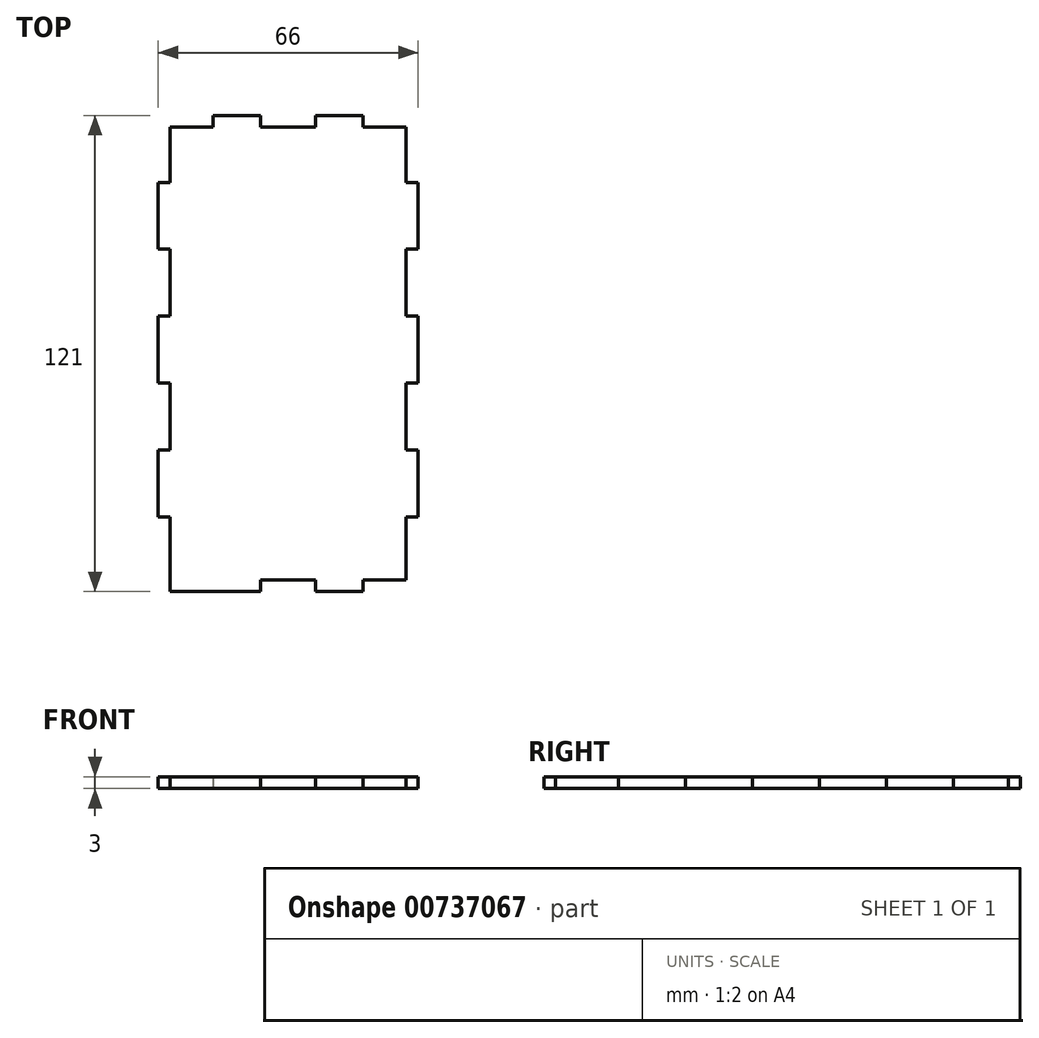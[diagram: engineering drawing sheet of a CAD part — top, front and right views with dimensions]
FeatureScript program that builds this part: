
annotation { "Feature Type Name" : "Feature", "Feature Type Description" : "" }
export const myFeature = defineFeature(function(context is Context, id is Id, definition is map)
    precondition{}
    {
        {
            var Q0;
            Q0=qCreatedBy(makeId("Top.planeOp"),FACE);
            var sketch = newSketch(context, id + "F0", { "sketchPlane" : qUnion([Q0])});
            skLineSegment(sketch, "E0.bottom", {"start": v(33, -60.5) * mm, "end": v(-33, -60.5) * mm, "construction": true});
            skLineSegment(sketch, "E0.top", {"start": v(33, 60.5) * mm, "end": v(-33, 60.5) * mm, "construction": true});
            skLineSegment(sketch, "E0.left", {"start": v(33, -60.5) * mm, "end": v(33, 60.5) * mm, "construction": true});
            skLineSegment(sketch, "E0.right", {"start": v(-33, -60.5) * mm, "end": v(-33, 60.5) * mm, "construction": true});
            skPoint(sketch, "E0.middle", {"position": v(0, 0) * mm});
            skLineSegment(sketch, "E1", {"start": v(-30, 57.5) * mm, "end": v(-19, 57.5) * mm});
            skLineSegment(sketch, "E2", {"start": v(-19, 57.5) * mm, "end": v(-19, 60.5) * mm});
            skLineSegment(sketch, "E3", {"start": v(-19, 60.5) * mm, "end": v(-7, 60.5) * mm});
            skLineSegment(sketch, "E4", {"start": v(-7, 60.5) * mm, "end": v(-7, 57.5) * mm});
            skLineSegment(sketch, "E5", {"start": v(-7, 57.5) * mm, "end": v(7, 57.5) * mm});
            skLineSegment(sketch, "E6", {"start": v(7, 57.5) * mm, "end": v(7, 60.5) * mm});
            skLineSegment(sketch, "E7", {"start": v(7, 60.5) * mm, "end": v(19, 60.5) * mm});
            skLineSegment(sketch, "E8", {"start": v(19, 60.5) * mm, "end": v(19, 57.5) * mm});
            skLineSegment(sketch, "E9", {"start": v(19, 57.5) * mm, "end": v(30, 57.5) * mm});
            skLineSegment(sketch, "E10", {"start": v(30, 57.5) * mm, "end": v(30, 43.5) * mm});
            skLineSegment(sketch, "E11", {"start": v(30, 43.5) * mm, "end": v(33, 43.5) * mm});
            skLineSegment(sketch, "E12", {"start": v(33, 43.5) * mm, "end": v(33, 26.5) * mm});
            skLineSegment(sketch, "E13", {"start": v(33, 26.5) * mm, "end": v(30, 26.5) * mm});
            skLineSegment(sketch, "E14", {"start": v(30, 26.5) * mm, "end": v(30, 9.5) * mm});
            skLineSegment(sketch, "E15", {"start": v(30, 9.5) * mm, "end": v(33, 9.5) * mm});
            skLineSegment(sketch, "E16", {"start": v(33, 9.5) * mm, "end": v(33, -7.5) * mm});
            skLineSegment(sketch, "E17", {"start": v(33, -7.5) * mm, "end": v(30, -7.5) * mm});
            skLineSegment(sketch, "E18", {"start": v(30, -7.5) * mm, "end": v(30, -24.5) * mm});
            skLineSegment(sketch, "E19", {"start": v(30, -24.5) * mm, "end": v(33, -24.5) * mm});
            skLineSegment(sketch, "E20", {"start": v(33, -24.5) * mm, "end": v(33, -41.5) * mm});
            skLineSegment(sketch, "E21", {"start": v(33, -41.5) * mm, "end": v(30, -41.5) * mm});
            skLineSegment(sketch, "E22", {"start": v(30, -41.5) * mm, "end": v(30, -57.5) * mm});
            skLineSegment(sketch, "E23", {"start": v(-30, 57.5) * mm, "end": v(-30, 43.5) * mm});
            skLineSegment(sketch, "E24", {"start": v(-30, 43.5) * mm, "end": v(-33, 43.5) * mm});
            skLineSegment(sketch, "E25", {"start": v(-33, 43.5) * mm, "end": v(-33, 26.5) * mm});
            skLineSegment(sketch, "E26", {"start": v(-33, 26.5) * mm, "end": v(-30, 26.5) * mm});
            skLineSegment(sketch, "E27", {"start": v(-30, 26.5) * mm, "end": v(-30, 9.5) * mm});
            skLineSegment(sketch, "E28", {"start": v(-30, 9.5) * mm, "end": v(-33, 9.5) * mm});
            skLineSegment(sketch, "E29", {"start": v(-33, 9.5) * mm, "end": v(-33, -7.5) * mm});
            skLineSegment(sketch, "E30", {"start": v(-33, -7.5) * mm, "end": v(-30, -7.5) * mm});
            skLineSegment(sketch, "E31", {"start": v(-30, -7.5) * mm, "end": v(-30, -24.5) * mm});
            skLineSegment(sketch, "E32", {"start": v(-30, -24.5) * mm, "end": v(-33, -24.5) * mm});
            skLineSegment(sketch, "E33", {"start": v(-33, -24.5) * mm, "end": v(-33, -41.5) * mm});
            skLineSegment(sketch, "E34", {"start": v(-33, -41.5) * mm, "end": v(-30, -41.5) * mm});
            skLineSegment(sketch, "E35", {"start": v(-30, -41.5) * mm, "end": v(-30, -60.5) * mm});
            skLineSegment(sketch, "E36", {"start": v(-30, -60.5) * mm, "end": v(-7, -60.5) * mm});
            skLineSegment(sketch, "E37", {"start": v(-7, -60.5) * mm, "end": v(-7, -57.5) * mm});
            skLineSegment(sketch, "E38", {"start": v(-7, -57.5) * mm, "end": v(7, -57.5) * mm});
            skLineSegment(sketch, "E39", {"start": v(7, -57.5) * mm, "end": v(7, -60.5) * mm});
            skLineSegment(sketch, "E40", {"start": v(7, -60.5) * mm, "end": v(19, -60.5) * mm});
            skLineSegment(sketch, "E41", {"start": v(19, -60.5) * mm, "end": v(19, -57.5) * mm});
            skLineSegment(sketch, "E42", {"start": v(19, -57.5) * mm, "end": v(30, -57.5) * mm});
            skSolve(sketch);
        }
        {
            var Q0;
            Q0=makeQuery(id+"F0.imprint","IMPRINT",FACE,{"disambiguationData":[TD([[makeQuery(id+"F0.imprint","IMPRINT",EDGE,{"derivedFrom":sQuery(id+"F0.wireOp",EDGE,"E1")}),-1.0]])]});
            extrude(context, id + "F1", {"entities" : qUnion([Q0]), "depth" : 3 * mm, "offsetDistance" : 25 * mm});
        }
    });
